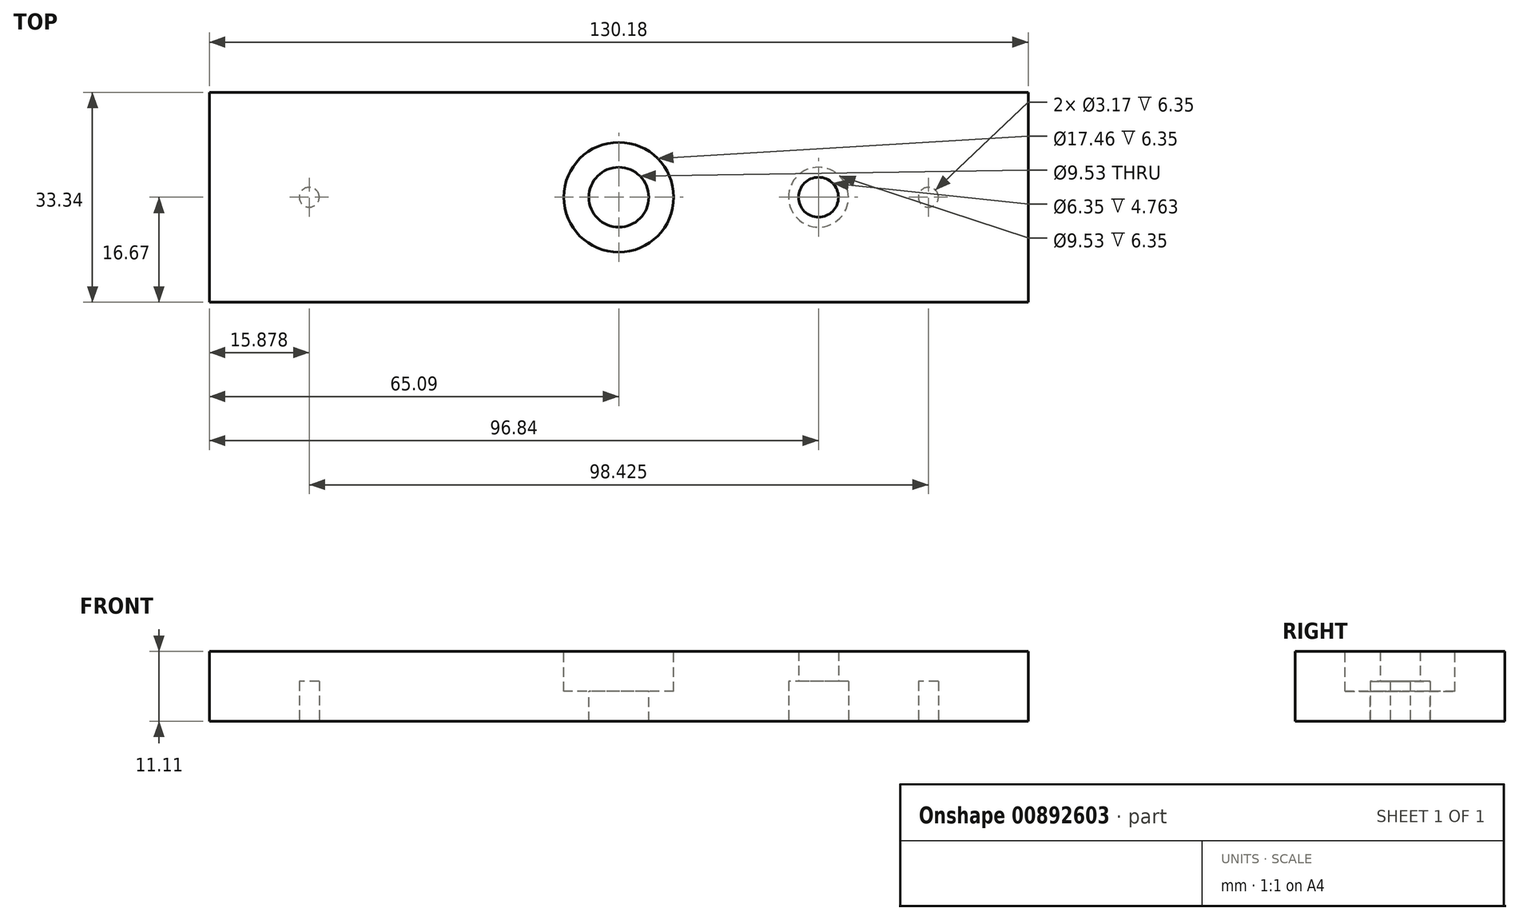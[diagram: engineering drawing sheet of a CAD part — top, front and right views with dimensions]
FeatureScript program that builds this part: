
annotation { "Feature Type Name" : "Feature", "Feature Type Description" : "" }
export const myFeature = defineFeature(function(context is Context, id is Id, definition is map)
    precondition{}
    {
        {
            var Q0;
            Q0=qCreatedBy(makeId("Top.planeOp"),FACE);
            var sketch = newSketch(context, id + "F0", { "sketchPlane" : qUnion([Q0])});
            skLineSegment(sketch, "E0.bottom", {"start": v(65.09, 16.67) * mm, "end": v(-65.09, 16.67) * mm});
            skLineSegment(sketch, "E0.top", {"start": v(65.09, -16.67) * mm, "end": v(-65.09, -16.67) * mm});
            skLineSegment(sketch, "E0.left", {"start": v(65.09, 16.67) * mm, "end": v(65.09, -16.67) * mm});
            skLineSegment(sketch, "E0.right", {"start": v(-65.09, 16.67) * mm, "end": v(-65.09, -16.67) * mm});
            skPoint(sketch, "E0.middle", {"position": v(0, 0) * mm});
            skSolve(sketch);
        }
        {
            var Q0;
            Q0 = qSketchRegion(id + "F0", true);
            extrude(context, id + "F1", {"entities" : qUnion([Q0]), "depth" : 11.1 * mm, "offsetDistance" : 25.4 * mm});
        }
        {
            var Q0;
            Q0=makeQuery(id+"F1.opExtrude","CAP_FACE",FACE,{"disambiguationData":[OSD([sQuery(id+"F0.wireOp",EDGE,"E0.bottom"),sQuery(id+"F0.wireOp",EDGE,"E0.top"),sQuery(id+"F0.wireOp",EDGE,"E0.left"),sQuery(id+"F0.wireOp",EDGE,"E0.right")])],"isStart":false});
            var sketch = newSketch(context, id + "F2", { "sketchPlane" : qUnion([Q0])});
            skCircle(sketch, "E1", {"center": v(0, 0) * mm, "radius": 8.73 * mm});
            skCircle(sketch, "E2", {"center": v(0, 0) * mm, "radius": 4.76 * mm});
            skSolve(sketch);
        }
        {
            var Q0;
            Q0 = qSketchRegion(id + "F2", true);
            extrude(context, id + "F3", {"entities" : qUnion([Q0]), "operationType" : NewBodyOperationType.REMOVE, "oppositeDirection" : true, "depth" : 6.35 * mm, "offsetDistance" : 25.4 * mm});
        }
        {
            var Q0;
            Q0=makeQuery(id+"F3.boolean.opBoolean","SPLIT",FACE,{"disambiguationData":[TD([makeQuery(id+"F3.opExtrude","SWEPT_FACE",FACE,{"disambiguationData":[OSD([sQuery(id+"F2.wireOp",EDGE,"E2")])]})])],"derivedFrom":makeQuery(id+"F1.opExtrude","CAP_FACE",FACE,{"disambiguationData":[OSD([sQuery(id+"F0.wireOp",EDGE,"E0.bottom"),sQuery(id+"F0.wireOp",EDGE,"E0.top"),sQuery(id+"F0.wireOp",EDGE,"E0.left"),sQuery(id+"F0.wireOp",EDGE,"E0.right")])],"isStart":false})});
            extrude(context, id + "F4", {"entities" : qUnion([Q0]), "operationType" : NewBodyOperationType.REMOVE, "endBound" : BoundingType.THROUGH_ALL, "oppositeDirection" : true, "depth" : 25.4 * mm, "offsetDistance" : 25.4 * mm});
        }
        {
            var Q0;
            Q0=makeQuery(id+"F0.imprint","IMPRINT",FACE,{"disambiguationData":[TD([[makeQuery(id+"F0.imprint","IMPRINT",EDGE,{"derivedFrom":sQuery(id+"F0.wireOp",EDGE,"E0.bottom")}),1.0]])]});
            var sketch = newSketch(context, id + "F5", { "sketchPlane" : qUnion([Q0])});
            skCircle(sketch, "E3", {"center": v(-49.21, 0) * mm, "radius": 1.59 * mm});
            skCircle(sketch, "E4", {"center": v(49.21, 0) * mm, "radius": 1.59 * mm});
            skCircle(sketch, "E5", {"center": v(31.75, 0) * mm, "radius": 4.76 * mm});
            skCircle(sketch, "E6", {"center": v(31.75, 0) * mm, "radius": 3.18 * mm});
            skSolve(sketch);
        }
        {
            var Q0;
            Q0=makeQuery(id+"F5.imprint","IMPRINT",FACE,{"disambiguationData":[TD([[makeQuery(id+"F5.imprint","IMPRINT",EDGE,{"derivedFrom":sQuery(id+"F5.wireOp",EDGE,"E3")}),1.0]])]});
            var Q1;
            Q1=makeQuery(id+"F5.imprint","IMPRINT",FACE,{"disambiguationData":[TD([[makeQuery(id+"F5.imprint","IMPRINT",EDGE,{"derivedFrom":sQuery(id+"F5.wireOp",EDGE,"E4")}),1.0]])]});
            extrude(context, id + "F6", {"entities" : qUnion([Q0, Q1]), "operationType" : NewBodyOperationType.REMOVE, "depth" : 6.35 * mm, "offsetDistance" : 25.4 * mm});
        }
        {
            var Q0;
            Q0=makeQuery(id+"F5.imprint","IMPRINT",FACE,{"disambiguationData":[TD([[makeQuery(id+"F5.imprint","IMPRINT",EDGE,{"derivedFrom":sQuery(id+"F5.wireOp",EDGE,"E6")}),1.0]])]});
            extrude(context, id + "F7", {"entities" : qUnion([Q0]), "operationType" : NewBodyOperationType.REMOVE, "endBound" : BoundingType.THROUGH_ALL, "depth" : 25.4 * mm, "offsetDistance" : 25.4 * mm});
        }
        {
            var Q0;
            Q0=makeQuery(id+"F5.imprint","IMPRINT",FACE,{"disambiguationData":[TD([[makeQuery(id+"F5.imprint","IMPRINT",EDGE,{"derivedFrom":sQuery(id+"F5.wireOp",EDGE,"E5")}),1.0]])]});
            extrude(context, id + "F8", {"entities" : qUnion([Q0]), "operationType" : NewBodyOperationType.REMOVE, "depth" : 6.35 * mm, "offsetDistance" : 25.4 * mm});
        }
    });
